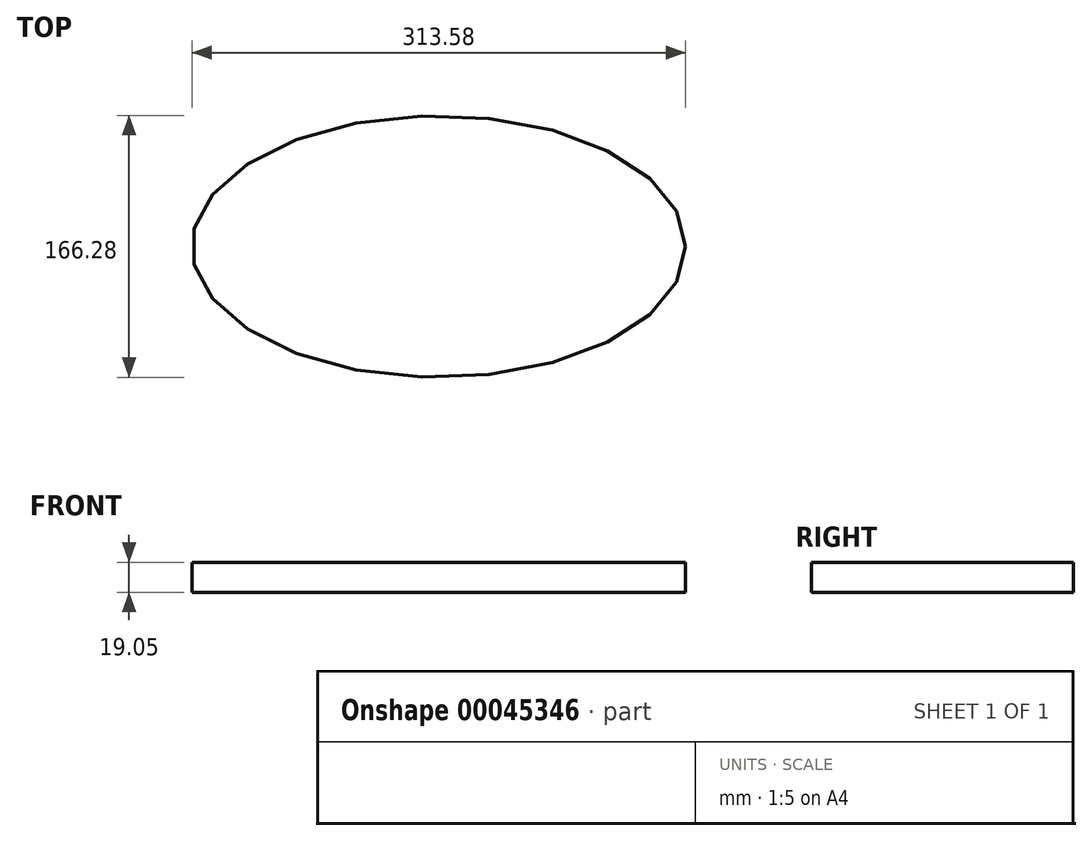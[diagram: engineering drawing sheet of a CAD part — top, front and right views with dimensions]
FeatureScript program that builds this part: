
annotation { "Feature Type Name" : "Feature", "Feature Type Description" : "" }
export const myFeature = defineFeature(function(context is Context, id is Id, definition is map)
    precondition{}
    {
        {
            var Q0;
            Q0=qCreatedBy(makeId("Top.planeOp"),FACE);
            var sketch = newSketch(context, id + "F0", { "sketchPlane" : qUnion([Q0])});
            skEllipse(sketch, "E0", {"center": v(0, 0) * mm, "majorRadius": 156.8 * mm, "minorRadius": 83.14 * mm, "majorAxis": v(1, 0)});
            skSolve(sketch);
        }
        {
            var Q0;
            Q0=makeQuery(id+"F0.imprint","IMPRINT",FACE,{"disambiguationData":[TD([[makeQuery(id+"F0.imprint","IMPRINT",EDGE,{"derivedFrom":sQuery(id+"F0.wireOp",EDGE,"E0")}),1.0]])]});
            extrude(context, id + "F1", {"entities" : qUnion([Q0]), "depth" : 19.05 * mm});
        }
    });
